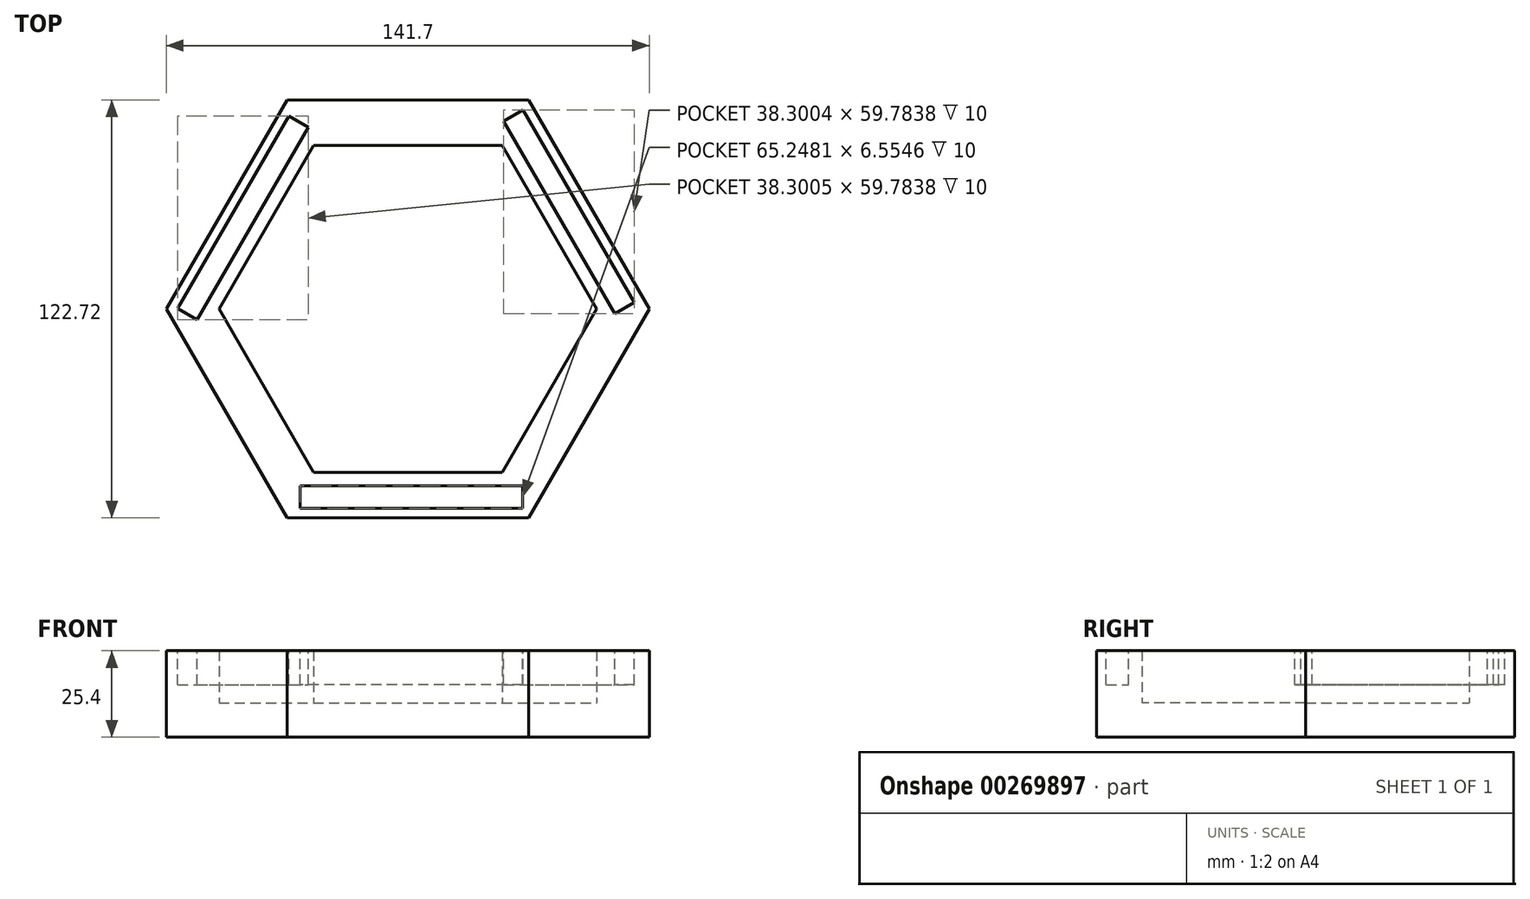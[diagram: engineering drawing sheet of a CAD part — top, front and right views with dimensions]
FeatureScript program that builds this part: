
annotation { "Feature Type Name" : "Feature", "Feature Type Description" : "" }
export const myFeature = defineFeature(function(context is Context, id is Id, definition is map)
    precondition{}
    {
        {
            var Q0;
            Q0=qCreatedBy(makeId("Top.planeOp"),FACE);
            var sketch = newSketch(context, id + "F0", { "sketchPlane" : qUnion([Q0])});
            skCircle(sketch, "E0.cCircle", {"center": v(0, 0) * mm, "radius": 61.36 * mm, "construction": true});
            skLineSegment(sketch, "E0.0", {"start": v(-35.43, 61.36) * mm, "end": v(35.43, 61.36) * mm});
            skLineSegment(sketch, "E0.1", {"start": v(35.43, 61.36) * mm, "end": v(70.85, 0) * mm});
            skLineSegment(sketch, "E0.2", {"start": v(70.85, 0) * mm, "end": v(35.43, -61.36) * mm});
            skLineSegment(sketch, "E0.3", {"start": v(35.43, -61.36) * mm, "end": v(-35.43, -61.36) * mm});
            skLineSegment(sketch, "E0.4", {"start": v(-35.43, -61.36) * mm, "end": v(-70.85, 0) * mm});
            skLineSegment(sketch, "E0.5", {"start": v(-70.85, 0) * mm, "end": v(-35.43, 61.36) * mm});
            skPoint(sketch, "E0.0.midPoint", {"position": v(0, 61.36) * mm});
            skCircle(sketch, "E1.cCircle", {"center": v(0, 0) * mm, "radius": 47.98 * mm, "construction": true});
            skLineSegment(sketch, "E1.0", {"start": v(-27.7, 47.98) * mm, "end": v(27.7, 47.98) * mm});
            skLineSegment(sketch, "E1.1", {"start": v(27.7, 47.98) * mm, "end": v(55.4, 0) * mm});
            skLineSegment(sketch, "E1.2", {"start": v(55.4, 0) * mm, "end": v(27.7, -47.98) * mm});
            skLineSegment(sketch, "E1.3", {"start": v(27.7, -47.98) * mm, "end": v(-27.7, -47.98) * mm});
            skLineSegment(sketch, "E1.4", {"start": v(-27.7, -47.98) * mm, "end": v(-55.4, 0) * mm});
            skLineSegment(sketch, "E1.5", {"start": v(-55.4, 0) * mm, "end": v(-27.7, 47.98) * mm});
            skPoint(sketch, "E1.0.midPoint", {"position": v(0, 47.98) * mm});
            skSolve(sketch);
        }
        {
            var Q0;
            Q0 = qSketchRegion(id + "F0", true);
            extrude(context, id + "F1", {"entities" : qUnion([Q0]), "depth" : 25.4 * mm});
        }
        {
            var Q0;
            Q0=makeQuery(id+"F1.opExtrude","CAP_FACE",FACE,{"disambiguationData":[OSD([sQuery(id+"F0.wireOp",EDGE,"E0.0"),sQuery(id+"F0.wireOp",EDGE,"E0.1"),sQuery(id+"F0.wireOp",EDGE,"E0.2"),sQuery(id+"F0.wireOp",EDGE,"E0.3"),sQuery(id+"F0.wireOp",EDGE,"E0.4"),sQuery(id+"F0.wireOp",EDGE,"E0.5"),sQuery(id+"F0.wireOp",EDGE,"E1.0"),sQuery(id+"F0.wireOp",EDGE,"E1.1"),sQuery(id+"F0.wireOp",EDGE,"E1.2"),sQuery(id+"F0.wireOp",EDGE,"E1.3"),sQuery(id+"F0.wireOp",EDGE,"E1.4"),sQuery(id+"F0.wireOp",EDGE,"E1.5")])],"isStart":false});
            var sketch = newSketch(context, id + "F2", { "sketchPlane" : qUnion([Q0])});
            skLineSegment(sketch, "E2.bottom", {"start": v(33.65, -58.49) * mm, "end": v(-31.6, -58.49) * mm});
            skLineSegment(sketch, "E2.top", {"start": v(33.65, -51.93) * mm, "end": v(-31.6, -51.93) * mm});
            skLineSegment(sketch, "E2.left", {"start": v(33.65, -58.49) * mm, "end": v(33.65, -51.93) * mm});
            skLineSegment(sketch, "E2.right", {"start": v(-31.6, -58.49) * mm, "end": v(-31.6, -51.93) * mm});
            skLineSegment(sketch, "E3.1.0", {"start": v(-67.48, 0.1) * mm, "end": v(-34.86, 56.6) * mm});
            skLineSegment(sketch, "E3.1.1", {"start": v(-61.8, -3.18) * mm, "end": v(-29.18, 53.33) * mm});
            skLineSegment(sketch, "E3.1.2", {"start": v(-67.48, 0.1) * mm, "end": v(-61.8, -3.18) * mm});
            skLineSegment(sketch, "E3.1.3", {"start": v(-34.86, 56.6) * mm, "end": v(-29.18, 53.33) * mm});
            skLineSegment(sketch, "E3.2.0", {"start": v(33.83, 58.39) * mm, "end": v(66.45, 1.88) * mm});
            skLineSegment(sketch, "E3.2.1", {"start": v(28.15, 55.11) * mm, "end": v(60.77, -1.4) * mm});
            skLineSegment(sketch, "E3.2.2", {"start": v(33.83, 58.39) * mm, "end": v(28.15, 55.11) * mm});
            skLineSegment(sketch, "E3.2.3", {"start": v(66.45, 1.88) * mm, "end": v(60.77, -1.4) * mm});
            skPoint(sketch, "E3.center", {"position": v(0, 0) * mm});
            skLineSegment(sketch, "E3.anchor1", {"start": v(0, 0) * mm, "end": v(-31.6, -58.49) * mm, "construction": true});
            skLineSegment(sketch, "E3.anchor2", {"start": v(0, 0) * mm, "end": v(66.45, 1.88) * mm, "construction": true});
            skSolve(sketch);
        }
        {
            var Q0;
            Q0=makeQuery(id+"F2.imprint","IMPRINT",FACE,{"disambiguationData":[TD([[makeQuery(id+"F2.imprint","IMPRINT",EDGE,{"derivedFrom":sQuery(id+"F2.wireOp",EDGE,"E3.2.0")}),-1.0]])]});
            var Q1;
            Q1=makeQuery(id+"F2.imprint","IMPRINT",FACE,{"disambiguationData":[TD([[makeQuery(id+"F2.imprint","IMPRINT",EDGE,{"derivedFrom":sQuery(id+"F2.wireOp",EDGE,"E2.bottom")}),-1.0]])]});
            var Q2;
            Q2=makeQuery(id+"F2.imprint","IMPRINT",FACE,{"disambiguationData":[TD([[makeQuery(id+"F2.imprint","IMPRINT",EDGE,{"derivedFrom":sQuery(id+"F2.wireOp",EDGE,"E3.1.0")}),-1.0]])]});
            extrude(context, id + "F3", {"entities" : qUnion([Q0, Q1, Q2]), "operationType" : NewBodyOperationType.REMOVE, "oppositeDirection" : true, "depth" : 10 * mm});
        }
        {
            var Q0;
            Q0=makeQuery(id+"F1.opExtrude","CAP_FACE",FACE,{"disambiguationData":[OSD([sQuery(id+"F0.wireOp",EDGE,"E0.0"),sQuery(id+"F0.wireOp",EDGE,"E0.1"),sQuery(id+"F0.wireOp",EDGE,"E0.2"),sQuery(id+"F0.wireOp",EDGE,"E0.3"),sQuery(id+"F0.wireOp",EDGE,"E0.4"),sQuery(id+"F0.wireOp",EDGE,"E0.5"),sQuery(id+"F0.wireOp",EDGE,"E1.0"),sQuery(id+"F0.wireOp",EDGE,"E1.1"),sQuery(id+"F0.wireOp",EDGE,"E1.2"),sQuery(id+"F0.wireOp",EDGE,"E1.3"),sQuery(id+"F0.wireOp",EDGE,"E1.4"),sQuery(id+"F0.wireOp",EDGE,"E1.5")])],"isStart":true});
            var sketch = newSketch(context, id + "F4", { "sketchPlane" : qUnion([Q0])});
            skLineSegment(sketch, "E4", {"start": v(-27.7, 47.98) * mm, "end": v(-28.83, 46.03) * mm});
            skLineSegment(sketch, "E5", {"start": v(-55.4, 0) * mm, "end": v(-27.7, -47.98) * mm});
            skLineSegment(sketch, "E6", {"start": v(-27.7, -47.98) * mm, "end": v(27.7, -47.98) * mm});
            skLineSegment(sketch, "E7", {"start": v(27.7, -47.98) * mm, "end": v(55.4, 0) * mm});
            skLineSegment(sketch, "E8", {"start": v(55.4, 0) * mm, "end": v(27.7, 47.98) * mm});
            skLineSegment(sketch, "E9", {"start": v(27.7, 47.98) * mm, "end": v(-27.7, 47.98) * mm});
            skLineSegment(sketch, "E10", {"start": v(-55.4, 0) * mm, "end": v(-27.7, 47.98) * mm});
            skSolve(sketch);
        }
        {
            var Q0;
            Q0 = qSketchRegion(id + "F4", true);
            extrude(context, id + "F5", {"entities" : qUnion([Q0]), "operationType" : NewBodyOperationType.ADD, "oppositeDirection" : true, "depth" : 10 * mm});
        }
    });
